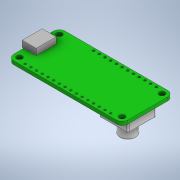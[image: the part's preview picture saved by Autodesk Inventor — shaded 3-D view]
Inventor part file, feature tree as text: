
AUTODESK INVENTOR PART (.ipt)
format: ipt  version: 2021 (Build 250183000, 183)  size: 260,096 bytes
history: native  units: in
note: dims shown in document units (in); Inventor stores cm internally (conversion verified against a paired STEP export)
features: extrude x7, sketch x7, pattern_linear x2, fillet x1, projected_geometry x1
ambient origin geometry x8: Origin, YZ Plane, XZ Plane, XY Plane, X Axis, Y Axis, Z Axis, Center Point
bodies: Solid1 (feature_tree)
feature tree (18):
  extrude  "Extrusion1"  Depth=0.9in
  extrude  "Extrusion4"  Depth=0.7in
  extrude  "Extrusion6"  Depth=0.1in
  pattern_linear  "Rectangular Pattern1"  Spacing1=0.063in  [1 undecoded]
  extrude  "Extrusion7"  Depth=0.025in
  pattern_linear  "Rectangular Pattern2"  Spacing1=0.245in  [1 undecoded]
  extrude  "Extrusion8"  Depth=0.11in TaperAngle=0.0deg
  extrude  "Extrusion9"  Depth=0.1181in
  fillet  "Fillet2"  Radius=0.05in
  extrude  "Extrusion10"  Depth=0.05in
  sketch  "Sketch1"  dims[d0=2.0in d1=0.9in]
  sketch  "Sketch4"  dims[d2=0.1in d6=0.7in]
  sketch  "Sketch6"  dims[d9=0.35in d10=0.1in]
  sketch  "Sketch7"  dims[d11=0.1in]
  sketch  "Sketch8"  dims[d13=0.1in]
  sketch  "Sketch9"  dims[d14=0.1in]
  sketch  "Sketch10"  dims[d15=0.1in d16=0.063in d17=0.0in d34=0.025in d35=0.245in d38=0.11in d39=0.0in d46=0.0394in d47=0.05in d48=0.05in d49=0.0in d50=0.0in d51=6.2992in d53=0.1in d54=1.15in d55=0.05in d56=0.0394in d57=0.0in d58=0.0in d59=4.7244in d61=0.1in d62=0.35in d63=0.5in d64=1.65in d65=0.25in d66=0.0in d67=0.28in d69=0.25in d70=0.0in d71=0.025in d72=0.32in d74=0.525in d75=0.1181in d76=0.0in]
  projected_geometry  "Project Cut Edges1"
note: 2 required parameter values undecoded (feature->parameter linkage not recoverable at this tier; creation-order binding heuristic only, values carry confidence <= 0.55)
